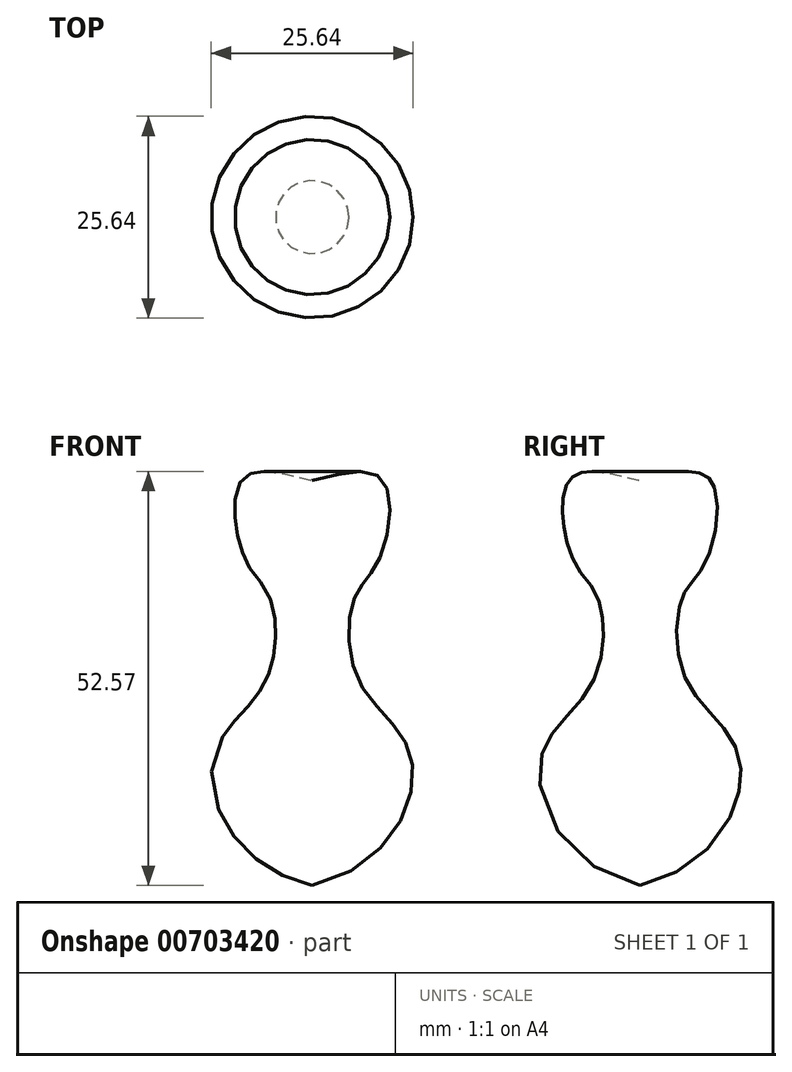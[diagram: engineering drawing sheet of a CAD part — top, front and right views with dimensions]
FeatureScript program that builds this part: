
annotation { "Feature Type Name" : "Feature", "Feature Type Description" : "" }
export const myFeature = defineFeature(function(context is Context, id is Id, definition is map)
    precondition{}
    {
        {
            var Q0;
            Q0=qCreatedBy(makeId("Front.planeOp"),FACE);
            var sketch = newSketch(context, id + "F0", { "sketchPlane" : qUnion([Q0])});
            skLineSegment(sketch, "E0", {"start": v(0, 0) * mm, "end": v(0, 51.43) * mm});
            skFitSpline(sketch, "E1", {"points": [v(0, 51.43) * mm, v(9.02, 51.43) * mm, v(8.36, 41.1) * mm, v(5.4, 36.64) * mm, v(6.07, 25.68) * mm, v(12.62, 16.1) * mm, v(0, 0) * mm], "startDerivative": vector(78.62, 20.23) * mm, "endDerivative": vector(-128.02, -28.07) * mm});
            skSolve(sketch);
        }
        {
            var Q0;
            Q0 = qSketchRegion(id + "F0", true);
            var Q1;
            Q1=sQuery(id+"F0.wireOp",EDGE,"E0");
            revolve(context, id + "F1", {"surfaceOperationType" : NewSurfaceOperationType.NEW, "entities" : qUnion([Q0]), "axis" : qUnion([Q1]), "revolveType" : RevolveType.FULL});
        }
    });
